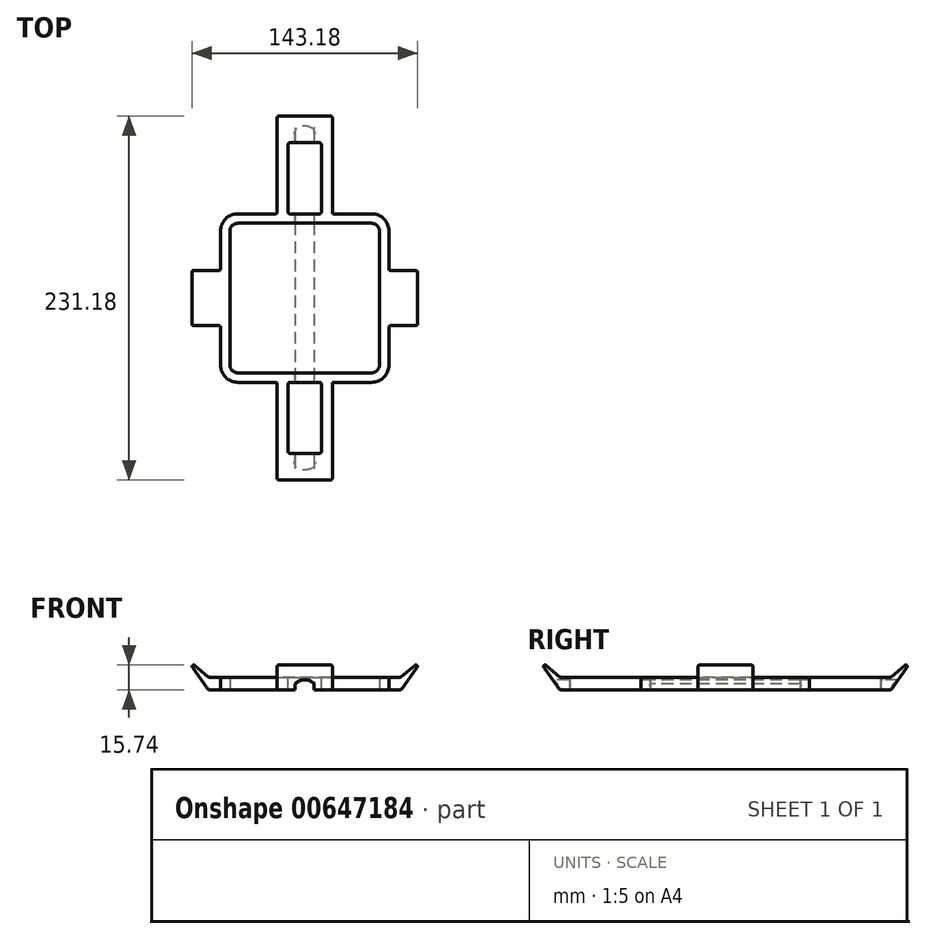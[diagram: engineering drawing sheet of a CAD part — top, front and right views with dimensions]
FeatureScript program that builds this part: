
annotation { "Feature Type Name" : "Feature", "Feature Type Description" : "" }
export const myFeature = defineFeature(function(context is Context, id is Id, definition is map)
    precondition{}
    {
        {
            var Q0;
            Q0=qCreatedBy(makeId("Top.planeOp"),FACE);
            var sketch = newSketch(context, id + "F0", { "sketchPlane" : qUnion([Q0])});
            skLineSegment(sketch, "E0.bottom", {"start": v(-42.5, -47.5) * mm, "end": v(42.5, -47.5) * mm});
            skLineSegment(sketch, "E0.top", {"start": v(-42.5, 47.5) * mm, "end": v(42.5, 47.5) * mm});
            skLineSegment(sketch, "E0.left", {"start": v(-47.5, -42.5) * mm, "end": v(-47.5, 42.5) * mm});
            skLineSegment(sketch, "E0.right", {"start": v(47.5, -42.5) * mm, "end": v(47.5, 42.5) * mm});
            skPoint(sketch, "E0.middle", {"position": v(0, 0) * mm});
            skPoint(sketch, "E1.visualSharp", {"position": v(-47.5, 47.5) * mm});
            skArc(sketch, "E1.filletArc", {"start": v(-42.5, 47.5) * mm, "mid": v(-46.04, 46.04) * mm, "end": v(-47.5, 42.5) * mm});
            skPoint(sketch, "E2.visualSharp", {"position": v(47.5, 47.5) * mm});
            skArc(sketch, "E2.filletArc", {"start": v(47.5, 42.5) * mm, "mid": v(46.04, 46.04) * mm, "end": v(42.5, 47.5) * mm});
            skPoint(sketch, "E3.visualSharp", {"position": v(47.5, -47.5) * mm});
            skArc(sketch, "E3.filletArc", {"start": v(42.5, -47.5) * mm, "mid": v(46.04, -46.04) * mm, "end": v(47.5, -42.5) * mm});
            skPoint(sketch, "E4.visualSharp", {"position": v(-47.5, -47.5) * mm});
            skArc(sketch, "E4.filletArc", {"start": v(-47.5, -42.5) * mm, "mid": v(-46.04, -46.04) * mm, "end": v(-42.5, -47.5) * mm});
            skSolve(sketch);
        }
        {
            var Q0;
            Q0=makeQuery(id+"F0.imprint","IMPRINT",FACE,{"disambiguationData":[TD([[makeQuery(id+"F0.imprint","IMPRINT",EDGE,{"derivedFrom":sQuery(id+"F0.wireOp",EDGE,"E0.bottom")}),1.0]])]});
            extrude(context, id + "F1", {"entities" : qUnion([Q0]), "depth" : 8 * mm, "offsetDistance" : 25 * mm});
        }
        {
            var Q0;
            Q0=qCreatedBy(makeId("Top.planeOp"),FACE);
            var sketch = newSketch(context, id + "F2", { "sketchPlane" : qUnion([Q0])});
            skLineSegment(sketch, "E5.bottom", {"start": v(17.5, -105) * mm, "end": v(-17.5, -105) * mm});
            skLineSegment(sketch, "E5.top", {"start": v(17.5, 105) * mm, "end": v(-17.5, 105) * mm});
            skLineSegment(sketch, "E5.left", {"start": v(17.5, -105) * mm, "end": v(17.5, -53.5) * mm});
            skLineSegment(sketch, "E5.right", {"start": v(-17.5, -105) * mm, "end": v(-17.5, -53.5) * mm});
            skPoint(sketch, "E5.middle", {"position": v(0, 0) * mm});
            skLineSegment(sketch, "E6.bottom", {"start": v(-61, 17.5) * mm, "end": v(-53.5, 17.5) * mm});
            skLineSegment(sketch, "E6.top", {"start": v(-61, -17.5) * mm, "end": v(-53.5, -17.5) * mm});
            skLineSegment(sketch, "E6.left", {"start": v(-61, 17.5) * mm, "end": v(-61, -17.5) * mm});
            skLineSegment(sketch, "E6.right", {"start": v(61, 17.5) * mm, "end": v(61, -17.5) * mm});
            skLineSegment(sketch, "E7.trimOffspring", {"start": v(53.5, 17.5) * mm, "end": v(61, 17.5) * mm});
            skLineSegment(sketch, "E8.trimOffspring", {"start": v(-17.5, 53.5) * mm, "end": v(-17.5, 105) * mm});
            skLineSegment(sketch, "E9.trimOffspring", {"start": v(17.5, 53.5) * mm, "end": v(17.5, 105) * mm});
            skLineSegment(sketch, "E10.trimOffspring", {"start": v(53.5, -17.5) * mm, "end": v(61, -17.5) * mm});
            skLineSegment(sketch, "E11.0", {"start": v(47.5, -42.5) * mm, "end": v(47.5, -17.5) * mm});
            skLineSegment(sketch, "E11.1", {"start": v(-47.5, -42.5) * mm, "end": v(-47.5, -17.5) * mm});
            skLineSegment(sketch, "E11.2", {"start": v(-42.5, -47.5) * mm, "end": v(-17.5, -47.5) * mm});
            skLineSegment(sketch, "E11.3", {"start": v(-42.5, 47.5) * mm, "end": v(-17.5, 47.5) * mm});
            skLineSegment(sketch, "E12.trimOffspring", {"start": v(47.5, 17.5) * mm, "end": v(47.5, 42.5) * mm});
            skLineSegment(sketch, "E13.trimOffspring", {"start": v(-47.5, 17.5) * mm, "end": v(-47.5, 42.5) * mm});
            skLineSegment(sketch, "E14.trimOffspring", {"start": v(17.5, -47.5) * mm, "end": v(42.5, -47.5) * mm});
            skLineSegment(sketch, "E15.trimOffspring", {"start": v(17.5, 47.5) * mm, "end": v(42.5, 47.5) * mm});
            skArc(sketch, "E16.0", {"start": v(-42.5, 47.5) * mm, "mid": v(-46.04, 46.04) * mm, "end": v(-47.5, 42.5) * mm});
            skArc(sketch, "E17.0", {"start": v(47.5, 42.5) * mm, "mid": v(46.04, 46.04) * mm, "end": v(42.5, 47.5) * mm});
            skPoint(sketch, "E18.0", {"position": v(46.04, -46.04) * mm});
            skArc(sketch, "E19.0", {"start": v(42.5, -47.5) * mm, "mid": v(46.04, -46.04) * mm, "end": v(47.5, -42.5) * mm});
            skArc(sketch, "E20.0", {"start": v(-47.5, -42.5) * mm, "mid": v(-46.04, -46.04) * mm, "end": v(-42.5, -47.5) * mm});
            skLineSegment(sketch, "E21.0", {"start": v(-42.5, 53.5) * mm, "end": v(-17.5, 53.5) * mm});
            skArc(sketch, "E21.1", {"start": v(-42.5, 53.5) * mm, "mid": v(-50.28, 50.28) * mm, "end": v(-53.5, 42.5) * mm});
            skLineSegment(sketch, "E21.2", {"start": v(-53.5, 17.5) * mm, "end": v(-53.5, 42.5) * mm});
            skLineSegment(sketch, "E22.0", {"start": v(53.5, 17.5) * mm, "end": v(53.5, 42.5) * mm});
            skArc(sketch, "E22.1", {"start": v(53.5, 42.5) * mm, "mid": v(50.28, 50.28) * mm, "end": v(42.5, 53.5) * mm});
            skLineSegment(sketch, "E22.2", {"start": v(17.5, 53.5) * mm, "end": v(42.5, 53.5) * mm});
            skLineSegment(sketch, "E23.0", {"start": v(53.5, -42.5) * mm, "end": v(53.5, -17.5) * mm});
            skArc(sketch, "E23.1", {"start": v(42.5, -53.5) * mm, "mid": v(50.28, -50.28) * mm, "end": v(53.5, -42.5) * mm});
            skLineSegment(sketch, "E23.2", {"start": v(17.5, -53.5) * mm, "end": v(42.5, -53.5) * mm});
            skLineSegment(sketch, "E24.0", {"start": v(-42.5, -53.5) * mm, "end": v(-17.5, -53.5) * mm});
            skArc(sketch, "E24.1", {"start": v(-53.5, -42.5) * mm, "mid": v(-50.28, -50.28) * mm, "end": v(-42.5, -53.5) * mm});
            skLineSegment(sketch, "E24.2", {"start": v(-53.5, -42.5) * mm, "end": v(-53.5, -17.5) * mm});
            skLineSegment(sketch, "E25", {"start": v(-17.5, 47.5) * mm, "end": v(17.5, 47.5) * mm});
            skLineSegment(sketch, "E26", {"start": v(47.5, 17.5) * mm, "end": v(47.5, -17.5) * mm});
            skLineSegment(sketch, "E27", {"start": v(-47.5, 17.5) * mm, "end": v(-47.5, -17.5) * mm});
            skLineSegment(sketch, "E28", {"start": v(-17.5, -47.5) * mm, "end": v(17.5, -47.5) * mm});
            skSolve(sketch);
        }
        {
            var Q0;
            Q0 = qSketchRegion(id + "F2", true);
            extrude(context, id + "F3", {"entities" : qUnion([Q0]), "depth" : 8 * mm, "offsetDistance" : 25 * mm});
        }
        {
            var Q0;
            Q0=makeQuery(id+"F3.opExtrude","SWEPT_FACE",FACE,{"disambiguationData":[OSD([sQuery(id+"F2.wireOp",EDGE,"E8.trimOffspring")])]});
            var sketch = newSketch(context, id + "F4", { "sketchPlane" : qUnion([Q0])});
            skLineSegment(sketch, "E29", {"start": v(-105, 8) * mm, "end": v(-120.32, 20.86) * mm});
            skLineSegment(sketch, "E30", {"start": v(-120.32, 20.86) * mm, "end": v(-105, 0) * mm});
            skLineSegment(sketch, "E31", {"start": v(0, 0) * mm, "end": v(0, 45.78) * mm, "construction": true});
            skLineSegment(sketch, "E32", {"start": v(-105, 8) * mm, "end": v(-105, 0) * mm});
            skLineSegment(sketch, "E33.MirrorCS", {"start": v(105, 8) * mm, "end": v(105, 0) * mm});
            skLineSegment(sketch, "E34.MirrorCS", {"start": v(120.32, 20.86) * mm, "end": v(120.32, 20.86) * mm});
            skLineSegment(sketch, "E35.MirrorCS", {"start": v(105, 8) * mm, "end": v(120.32, 20.86) * mm});
            skLineSegment(sketch, "E36.MirrorCS", {"start": v(120.32, 20.86) * mm, "end": v(105, 0) * mm});
            skSolve(sketch);
        }
        {
            var Q0;
            Q0 = qSketchRegion(id + "F4", true);
            extrude(context, id + "F5", {"entities" : qUnion([Q0]), "operationType" : NewBodyOperationType.ADD, "oppositeDirection" : true, "depth" : 35 * mm, "offsetDistance" : 25 * mm});
        }
        {
            var Q0;
            Q0=makeQuery(id+"F3.opExtrude","SWEPT_FACE",FACE,{"disambiguationData":[OSD([sQuery(id+"F2.wireOp",EDGE,"E6.top")])]});
            var sketch = newSketch(context, id + "F6", { "sketchPlane" : qUnion([Q0])});
            skLineSegment(sketch, "E37", {"start": v(0, 0) * mm, "end": v(0, 33.48) * mm, "construction": true});
            skLineSegment(sketch, "E38", {"start": v(-61, 8) * mm, "end": v(-76.32, 20.86) * mm});
            skLineSegment(sketch, "E39", {"start": v(-76.32, 20.86) * mm, "end": v(-61, 0) * mm});
            skLineSegment(sketch, "E40", {"start": v(-61, 0) * mm, "end": v(-61, 8) * mm});
            skLineSegment(sketch, "E41.MirrorCS", {"start": v(76.32, 20.86) * mm, "end": v(61, 0) * mm});
            skLineSegment(sketch, "E42.MirrorCS", {"start": v(61, 0) * mm, "end": v(61, 8) * mm});
            skLineSegment(sketch, "E43.MirrorCS", {"start": v(61, 8) * mm, "end": v(76.32, 20.86) * mm});
            skSolve(sketch);
        }
        {
            var Q0;
            Q0 = qSketchRegion(id + "F6", true);
            extrude(context, id + "F7", {"entities" : qUnion([Q0]), "operationType" : NewBodyOperationType.ADD, "oppositeDirection" : true, "depth" : 35 * mm, "offsetDistance" : 25 * mm});
        }
        {
            var Q0;
            Q0=makeQuery(id+"F3.opExtrude","SWEPT_FACE",FACE,{"disambiguationData":[OSD([sQuery(id+"F2.wireOp",EDGE,"E11.2"),sQuery(id+"F2.wireOp",EDGE,"E14.trimOffspring"),sQuery(id+"F2.wireOp",EDGE,"E28")])]});
            var sketch = newSketch(context, id + "F8", { "sketchPlane" : qUnion([Q0])});
            skLineSegment(sketch, "E44", {"start": v(-6, 0) * mm, "end": v(-6, 3.78) * mm});
            skLineSegment(sketch, "E45", {"start": v(-6, 0) * mm, "end": v(6, 0) * mm});
            skLineSegment(sketch, "E46", {"start": v(6, 0) * mm, "end": v(6, 3.78) * mm});
            skLineSegment(sketch, "E47", {"start": v(0, 0) * mm, "end": v(0, 8) * mm, "construction": true});
            skArc(sketch, "E48", {"start": v(6, 3.78) * mm, "mid": v(0, 6.4) * mm, "end": v(-6, 3.78) * mm});
            skSolve(sketch);
        }
        {
            var Q0;
            Q0 = qSketchRegion(id + "F8", true);
            extrude(context, id + "F9", {"entities" : qUnion([Q0]), "operationType" : NewBodyOperationType.REMOVE, "endBound" : BoundingType.SYMMETRIC, "depth" : 500 * mm, "offsetDistance" : 25 * mm});
        }
        {
            var Q0;
            Q0=makeQuery(id+"F9.boolean.opBoolean","COPY",FACE,{"disambiguationData":[TD([makeQuery(id+"F5.opExtrude","SWEPT_FACE",FACE,{"disambiguationData":[OSD([sQuery(id+"F4.wireOp",EDGE,"E30")])]})])],"derivedFrom":makeQuery(id+"F9.opExtrude","SWEPT_FACE",FACE,{"disambiguationData":[OSD([sQuery(id+"F8.wireOp",EDGE,"E48")])]})});
            var Q1;
            Q1=makeQuery(id+"F9.boolean.opBoolean","COPY",FACE,{"disambiguationData":[TD([makeQuery(id+"F5.opExtrude","SWEPT_FACE",FACE,{"disambiguationData":[OSD([sQuery(id+"F4.wireOp",EDGE,"E36.MirrorCS")])]})])],"derivedFrom":makeQuery(id+"F9.opExtrude","SWEPT_FACE",FACE,{"disambiguationData":[OSD([sQuery(id+"F8.wireOp",EDGE,"E48")])]})});
            fillet(context, id + "F10", {"entities" : qUnion([Q0, Q1]), "radius" : 1 * mm, "tangentPropagation" : true, "allowEdgeOverflow" : false});
        }
        {
            var Q0;
            Q0=makeQuery(id+"F7.opExtrude","SWEPT_EDGE",EDGE,{"disambiguationData":[OSD([sQuery(id+"F6.wireOp",EDGE,"E38"),sQuery(id+"F6.wireOp",EDGE,"E39")])]});
            var Q1;
            Q1=makeQuery(id+"F5.opExtrude","SWEPT_EDGE",EDGE,{"disambiguationData":[OSD([sQuery(id+"F4.wireOp",EDGE,"E35.MirrorCS"),sQuery(id+"F4.wireOp",EDGE,"E36.MirrorCS")])]});
            var Q2;
            Q2=makeQuery(id+"F7.opExtrude","SWEPT_EDGE",EDGE,{"disambiguationData":[OSD([sQuery(id+"F6.wireOp",EDGE,"E41.MirrorCS"),sQuery(id+"F6.wireOp",EDGE,"E43.MirrorCS")])]});
            var Q3;
            Q3=makeQuery(id+"F5.opExtrude","SWEPT_EDGE",EDGE,{"disambiguationData":[OSD([sQuery(id+"F4.wireOp",EDGE,"E29"),sQuery(id+"F4.wireOp",EDGE,"E30")])]});
            fillet(context, id + "F11", {"entities" : qUnion([Q0, Q1, Q2, Q3]), "radius" : 1 * mm, "tangentPropagation" : true, "allowEdgeOverflow" : false});
        }
        {
            var Q0;
            Q0=makeQuery(id+"F3.opExtrude","CAP_FACE",FACE,{"disambiguationData":[OSD([sQuery(id+"F2.wireOp",EDGE,"E5.bottom"),sQuery(id+"F2.wireOp",EDGE,"E5.top"),sQuery(id+"F2.wireOp",EDGE,"E5.left"),sQuery(id+"F2.wireOp",EDGE,"E5.right"),sQuery(id+"F2.wireOp",EDGE,"E6.bottom"),sQuery(id+"F2.wireOp",EDGE,"E6.top"),sQuery(id+"F2.wireOp",EDGE,"E6.left"),sQuery(id+"F2.wireOp",EDGE,"E6.right"),sQuery(id+"F2.wireOp",EDGE,"E7.trimOffspring"),sQuery(id+"F2.wireOp",EDGE,"E8.trimOffspring"),sQuery(id+"F2.wireOp",EDGE,"E9.trimOffspring"),sQuery(id+"F2.wireOp",EDGE,"E10.trimOffspring"),sQuery(id+"F2.wireOp",EDGE,"E11.0"),sQuery(id+"F2.wireOp",EDGE,"E11.1"),sQuery(id+"F2.wireOp",EDGE,"E11.2"),sQuery(id+"F2.wireOp",EDGE,"E11.3"),sQuery(id+"F2.wireOp",EDGE,"E12.trimOffspring"),sQuery(id+"F2.wireOp",EDGE,"E13.trimOffspring"),sQuery(id+"F2.wireOp",EDGE,"E14.trimOffspring"),sQuery(id+"F2.wireOp",EDGE,"E15.trimOffspring"),sQuery(id+"F2.wireOp",EDGE,"E16.0"),sQuery(id+"F2.wireOp",EDGE,"E17.0"),sQuery(id+"F2.wireOp",EDGE,"E19.0"),sQuery(id+"F2.wireOp",EDGE,"E20.0"),sQuery(id+"F2.wireOp",EDGE,"E21.0"),sQuery(id+"F2.wireOp",EDGE,"E21.1"),sQuery(id+"F2.wireOp",EDGE,"E21.2"),sQuery(id+"F2.wireOp",EDGE,"E22.0"),sQuery(id+"F2.wireOp",EDGE,"E22.1"),sQuery(id+"F2.wireOp",EDGE,"E22.2"),sQuery(id+"F2.wireOp",EDGE,"E23.0"),sQuery(id+"F2.wireOp",EDGE,"E23.1"),sQuery(id+"F2.wireOp",EDGE,"E23.2"),sQuery(id+"F2.wireOp",EDGE,"E24.0"),sQuery(id+"F2.wireOp",EDGE,"E24.1"),sQuery(id+"F2.wireOp",EDGE,"E24.2"),sQuery(id+"F2.wireOp",EDGE,"E25"),sQuery(id+"F2.wireOp",EDGE,"E26"),sQuery(id+"F2.wireOp",EDGE,"E27"),sQuery(id+"F2.wireOp",EDGE,"E28")])],"isStart":false});
            var Q1;
            Q1=makeQuery(id+"F3.opExtrude","CAP_FACE",FACE,{"disambiguationData":[OSD([sQuery(id+"F2.wireOp",EDGE,"E5.bottom"),sQuery(id+"F2.wireOp",EDGE,"E5.top"),sQuery(id+"F2.wireOp",EDGE,"E5.left"),sQuery(id+"F2.wireOp",EDGE,"E5.right"),sQuery(id+"F2.wireOp",EDGE,"E6.bottom"),sQuery(id+"F2.wireOp",EDGE,"E6.top"),sQuery(id+"F2.wireOp",EDGE,"E6.left"),sQuery(id+"F2.wireOp",EDGE,"E6.right"),sQuery(id+"F2.wireOp",EDGE,"E7.trimOffspring"),sQuery(id+"F2.wireOp",EDGE,"E8.trimOffspring"),sQuery(id+"F2.wireOp",EDGE,"E9.trimOffspring"),sQuery(id+"F2.wireOp",EDGE,"E10.trimOffspring"),sQuery(id+"F2.wireOp",EDGE,"E11.0"),sQuery(id+"F2.wireOp",EDGE,"E11.1"),sQuery(id+"F2.wireOp",EDGE,"E11.2"),sQuery(id+"F2.wireOp",EDGE,"E11.3"),sQuery(id+"F2.wireOp",EDGE,"E12.trimOffspring"),sQuery(id+"F2.wireOp",EDGE,"E13.trimOffspring"),sQuery(id+"F2.wireOp",EDGE,"E14.trimOffspring"),sQuery(id+"F2.wireOp",EDGE,"E15.trimOffspring"),sQuery(id+"F2.wireOp",EDGE,"E16.0"),sQuery(id+"F2.wireOp",EDGE,"E17.0"),sQuery(id+"F2.wireOp",EDGE,"E19.0"),sQuery(id+"F2.wireOp",EDGE,"E20.0"),sQuery(id+"F2.wireOp",EDGE,"E21.0"),sQuery(id+"F2.wireOp",EDGE,"E21.1"),sQuery(id+"F2.wireOp",EDGE,"E21.2"),sQuery(id+"F2.wireOp",EDGE,"E22.0"),sQuery(id+"F2.wireOp",EDGE,"E22.1"),sQuery(id+"F2.wireOp",EDGE,"E22.2"),sQuery(id+"F2.wireOp",EDGE,"E23.0"),sQuery(id+"F2.wireOp",EDGE,"E23.1"),sQuery(id+"F2.wireOp",EDGE,"E23.2"),sQuery(id+"F2.wireOp",EDGE,"E24.0"),sQuery(id+"F2.wireOp",EDGE,"E24.1"),sQuery(id+"F2.wireOp",EDGE,"E24.2"),sQuery(id+"F2.wireOp",EDGE,"E25"),sQuery(id+"F2.wireOp",EDGE,"E26"),sQuery(id+"F2.wireOp",EDGE,"E27"),sQuery(id+"F2.wireOp",EDGE,"E28")])],"isStart":true});
            var Q2;
            Q2=makeQuery(id+"F5.boolean.opBoolean","MERGE",FACE,{"derivedFrom":[makeQuery(id+"F3.opExtrude","SWEPT_FACE",FACE,{"disambiguationData":[OSD([sQuery(id+"F2.wireOp",EDGE,"E8.trimOffspring")])]}),makeQuery(id+"F5.opExtrude","CAP_FACE",FACE,{"disambiguationData":[OSD([sQuery(id+"F4.wireOp",EDGE,"E29"),sQuery(id+"F4.wireOp",EDGE,"E30"),sQuery(id+"F4.wireOp",EDGE,"E32")])],"isStart":true})]});
            var Q3;
            Q3=makeQuery(id+"F7.boolean.opBoolean","MERGE",FACE,{"derivedFrom":[makeQuery(id+"F3.opExtrude","SWEPT_FACE",FACE,{"disambiguationData":[OSD([sQuery(id+"F2.wireOp",EDGE,"E6.bottom")])]}),makeQuery(id+"F7.opExtrude","CAP_FACE",FACE,{"disambiguationData":[OSD([sQuery(id+"F6.wireOp",EDGE,"E38"),sQuery(id+"F6.wireOp",EDGE,"E39"),sQuery(id+"F6.wireOp",EDGE,"E40")])],"isStart":false})]});
            var Q4;
            Q4=makeQuery(id+"F7.boolean.opBoolean","MERGE",FACE,{"derivedFrom":[makeQuery(id+"F3.opExtrude","SWEPT_FACE",FACE,{"disambiguationData":[OSD([sQuery(id+"F2.wireOp",EDGE,"E6.top")])]}),makeQuery(id+"F7.opExtrude","CAP_FACE",FACE,{"disambiguationData":[OSD([sQuery(id+"F6.wireOp",EDGE,"E38"),sQuery(id+"F6.wireOp",EDGE,"E39"),sQuery(id+"F6.wireOp",EDGE,"E40")])],"isStart":true})]});
            var Q5;
            Q5=makeQuery(id+"F5.boolean.opBoolean","MERGE",FACE,{"derivedFrom":[makeQuery(id+"F3.opExtrude","SWEPT_FACE",FACE,{"disambiguationData":[OSD([sQuery(id+"F2.wireOp",EDGE,"E5.right")])]}),makeQuery(id+"F5.opExtrude","CAP_FACE",FACE,{"disambiguationData":[OSD([sQuery(id+"F4.wireOp",EDGE,"E33.MirrorCS"),sQuery(id+"F4.wireOp",EDGE,"E35.MirrorCS"),sQuery(id+"F4.wireOp",EDGE,"E36.MirrorCS")])],"isStart":true})]});
            var Q6;
            Q6=makeQuery(id+"F5.boolean.opBoolean","MERGE",FACE,{"derivedFrom":[makeQuery(id+"F3.opExtrude","SWEPT_FACE",FACE,{"disambiguationData":[OSD([sQuery(id+"F2.wireOp",EDGE,"E5.left")])]}),makeQuery(id+"F5.opExtrude","CAP_FACE",FACE,{"disambiguationData":[OSD([sQuery(id+"F4.wireOp",EDGE,"E33.MirrorCS"),sQuery(id+"F4.wireOp",EDGE,"E35.MirrorCS"),sQuery(id+"F4.wireOp",EDGE,"E36.MirrorCS")])],"isStart":false})]});
            var Q7;
            Q7=makeQuery(id+"F7.boolean.opBoolean","MERGE",FACE,{"derivedFrom":[makeQuery(id+"F3.opExtrude","SWEPT_FACE",FACE,{"disambiguationData":[OSD([sQuery(id+"F2.wireOp",EDGE,"E10.trimOffspring")])]}),makeQuery(id+"F7.opExtrude","CAP_FACE",FACE,{"disambiguationData":[OSD([sQuery(id+"F6.wireOp",EDGE,"E41.MirrorCS"),sQuery(id+"F6.wireOp",EDGE,"E42.MirrorCS"),sQuery(id+"F6.wireOp",EDGE,"E43.MirrorCS")])],"isStart":true})]});
            var Q8;
            Q8=makeQuery(id+"F7.boolean.opBoolean","MERGE",FACE,{"derivedFrom":[makeQuery(id+"F3.opExtrude","SWEPT_FACE",FACE,{"disambiguationData":[OSD([sQuery(id+"F2.wireOp",EDGE,"E7.trimOffspring")])]}),makeQuery(id+"F7.opExtrude","CAP_FACE",FACE,{"disambiguationData":[OSD([sQuery(id+"F6.wireOp",EDGE,"E41.MirrorCS"),sQuery(id+"F6.wireOp",EDGE,"E42.MirrorCS"),sQuery(id+"F6.wireOp",EDGE,"E43.MirrorCS")])],"isStart":false})]});
            var Q9;
            Q9=makeQuery(id+"F5.boolean.opBoolean","MERGE",FACE,{"derivedFrom":[makeQuery(id+"F3.opExtrude","SWEPT_FACE",FACE,{"disambiguationData":[OSD([sQuery(id+"F2.wireOp",EDGE,"E9.trimOffspring")])]}),makeQuery(id+"F5.opExtrude","CAP_FACE",FACE,{"disambiguationData":[OSD([sQuery(id+"F4.wireOp",EDGE,"E29"),sQuery(id+"F4.wireOp",EDGE,"E30"),sQuery(id+"F4.wireOp",EDGE,"E32")])],"isStart":false})]});
            fillet(context, id + "F12", {"entities" : qUnion([Q0, Q1, Q2, Q3, Q4, Q5, Q6, Q7, Q8, Q9]), "radius" : 1 * mm, "tangentPropagation" : true, "allowEdgeOverflow" : false});
        }
        {
            var Q0;
            Q0=makeQuery(id+"F3.opExtrude","CAP_FACE",FACE,{"disambiguationData":[OSD([sQuery(id+"F2.wireOp",EDGE,"E5.bottom"),sQuery(id+"F2.wireOp",EDGE,"E5.top"),sQuery(id+"F2.wireOp",EDGE,"E5.left"),sQuery(id+"F2.wireOp",EDGE,"E5.right"),sQuery(id+"F2.wireOp",EDGE,"E6.bottom"),sQuery(id+"F2.wireOp",EDGE,"E6.top"),sQuery(id+"F2.wireOp",EDGE,"E6.left"),sQuery(id+"F2.wireOp",EDGE,"E6.right"),sQuery(id+"F2.wireOp",EDGE,"E7.trimOffspring"),sQuery(id+"F2.wireOp",EDGE,"E8.trimOffspring"),sQuery(id+"F2.wireOp",EDGE,"E9.trimOffspring"),sQuery(id+"F2.wireOp",EDGE,"E10.trimOffspring"),sQuery(id+"F2.wireOp",EDGE,"E11.0"),sQuery(id+"F2.wireOp",EDGE,"E11.1"),sQuery(id+"F2.wireOp",EDGE,"E11.2"),sQuery(id+"F2.wireOp",EDGE,"E11.3"),sQuery(id+"F2.wireOp",EDGE,"E12.trimOffspring"),sQuery(id+"F2.wireOp",EDGE,"E13.trimOffspring"),sQuery(id+"F2.wireOp",EDGE,"E14.trimOffspring"),sQuery(id+"F2.wireOp",EDGE,"E15.trimOffspring"),sQuery(id+"F2.wireOp",EDGE,"E16.0"),sQuery(id+"F2.wireOp",EDGE,"E17.0"),sQuery(id+"F2.wireOp",EDGE,"E19.0"),sQuery(id+"F2.wireOp",EDGE,"E20.0"),sQuery(id+"F2.wireOp",EDGE,"E21.0"),sQuery(id+"F2.wireOp",EDGE,"E21.1"),sQuery(id+"F2.wireOp",EDGE,"E21.2"),sQuery(id+"F2.wireOp",EDGE,"E22.0"),sQuery(id+"F2.wireOp",EDGE,"E22.1"),sQuery(id+"F2.wireOp",EDGE,"E22.2"),sQuery(id+"F2.wireOp",EDGE,"E23.0"),sQuery(id+"F2.wireOp",EDGE,"E23.1"),sQuery(id+"F2.wireOp",EDGE,"E23.2"),sQuery(id+"F2.wireOp",EDGE,"E24.0"),sQuery(id+"F2.wireOp",EDGE,"E24.1"),sQuery(id+"F2.wireOp",EDGE,"E24.2"),sQuery(id+"F2.wireOp",EDGE,"E25"),sQuery(id+"F2.wireOp",EDGE,"E26"),sQuery(id+"F2.wireOp",EDGE,"E27"),sQuery(id+"F2.wireOp",EDGE,"E28")])],"isStart":false});
            var sketch = newSketch(context, id + "F13", { "sketchPlane" : qUnion([Q0])});
            skLineSegment(sketch, "E49.bottom", {"start": v(-10.5, 98.64) * mm, "end": v(10.5, 98.64) * mm});
            skLineSegment(sketch, "E49.top", {"start": v(-10.5, 53.5) * mm, "end": v(10.5, 53.5) * mm});
            skLineSegment(sketch, "E49.left", {"start": v(-10.5, 98.64) * mm, "end": v(-10.5, 53.5) * mm});
            skLineSegment(sketch, "E49.right", {"start": v(10.5, 98.64) * mm, "end": v(10.5, 53.5) * mm});
            skLineSegment(sketch, "E50", {"start": v(0, 0) * mm, "end": v(36.43, 0) * mm, "construction": true});
            skLineSegment(sketch, "E51.MirrorCS", {"start": v(-10.5, -98.64) * mm, "end": v(10.5, -98.64) * mm});
            skLineSegment(sketch, "E52.MirrorCS", {"start": v(-10.5, -53.5) * mm, "end": v(10.5, -53.5) * mm});
            skLineSegment(sketch, "E53.MirrorCS", {"start": v(-10.5, -98.64) * mm, "end": v(-10.5, -53.5) * mm});
            skLineSegment(sketch, "E54.MirrorCS", {"start": v(10.5, -98.64) * mm, "end": v(10.5, -53.5) * mm});
            skSolve(sketch);
        }
        {
            var Q0;
            Q0 = qSketchRegion(id + "F13", true);
            extrude(context, id + "F14", {"entities" : qUnion([Q0]), "operationType" : NewBodyOperationType.REMOVE, "flatOperationType" : FlatOperationType.REMOVE, "endBound" : BoundingType.THROUGH_ALL, "oppositeDirection" : true, "depth" : 25 * mm, "offsetDistance" : 25 * mm, "domain" : OperationDomain.MODEL});
        }
        {
            var Q0;
            Q0=makeQuery(id+"F14.boolean.opBoolean","COPY",FACE,{"derivedFrom":makeQuery(id+"F14.opExtrude","SWEPT_FACE",FACE,{"disambiguationData":[OSD([sQuery(id+"F13.wireOp",EDGE,"E49.bottom")])]})});
            var Q1;
            Q1=makeQuery(id+"F14.boolean.opBoolean","COPY",FACE,{"derivedFrom":makeQuery(id+"F14.opExtrude","SWEPT_FACE",FACE,{"disambiguationData":[OSD([sQuery(id+"F13.wireOp",EDGE,"E49.right")])]})});
            var Q2;
            Q2=makeQuery(id+"F14.boolean.opBoolean","COPY",FACE,{"derivedFrom":makeQuery(id+"F14.opExtrude","SWEPT_FACE",FACE,{"disambiguationData":[OSD([sQuery(id+"F13.wireOp",EDGE,"E49.top")])]})});
            var Q3;
            Q3=makeQuery(id+"F14.boolean.opBoolean","COPY",FACE,{"derivedFrom":makeQuery(id+"F14.opExtrude","SWEPT_FACE",FACE,{"disambiguationData":[OSD([sQuery(id+"F13.wireOp",EDGE,"E49.left")])]})});
            var Q4;
            Q4=makeQuery(id+"F14.boolean.opBoolean","COPY",FACE,{"derivedFrom":makeQuery(id+"F14.opExtrude","SWEPT_FACE",FACE,{"disambiguationData":[OSD([sQuery(id+"F13.wireOp",EDGE,"E52.MirrorCS")])]})});
            var Q5;
            Q5=makeQuery(id+"F14.boolean.opBoolean","COPY",FACE,{"derivedFrom":makeQuery(id+"F14.opExtrude","SWEPT_FACE",FACE,{"disambiguationData":[OSD([sQuery(id+"F13.wireOp",EDGE,"E54.MirrorCS")])]})});
            var Q6;
            Q6=makeQuery(id+"F14.boolean.opBoolean","COPY",FACE,{"derivedFrom":makeQuery(id+"F14.opExtrude","SWEPT_FACE",FACE,{"disambiguationData":[OSD([sQuery(id+"F13.wireOp",EDGE,"E51.MirrorCS")])]})});
            var Q7;
            Q7=makeQuery(id+"F14.boolean.opBoolean","COPY",FACE,{"derivedFrom":makeQuery(id+"F14.opExtrude","SWEPT_FACE",FACE,{"disambiguationData":[OSD([sQuery(id+"F13.wireOp",EDGE,"E53.MirrorCS")])]})});
            fillet(context, id + "F15", {"entities" : qUnion([Q0, Q1, Q2, Q3, Q4, Q5, Q6, Q7]), "radius" : 1 * mm, "tangentPropagation" : true, "allowEdgeOverflow" : false});
        }
    });
